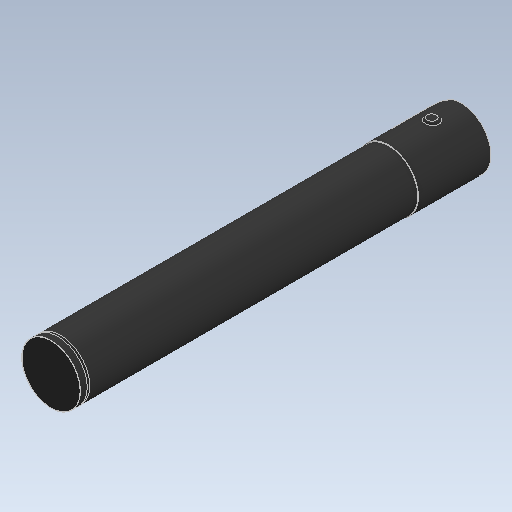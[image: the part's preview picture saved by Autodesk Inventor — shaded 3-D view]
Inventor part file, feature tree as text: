
AUTODESK INVENTOR PART (.ipt)
format: ipt  version: 2021 (Build 250183000, 183)  size: 203,264 bytes
history: native  units: mm
features: extrude x6, sketch x6, fillet x4, plane x1, projected_geometry x1
ambient origin geometry x8: Origin, YZ Plane, XZ Plane, XY Plane, X Axis, Y Axis, Z Axis, Center Point
bodies: Solid1 (feature_tree)
feature tree (18):
  extrude  "Extrusion1"  Depth=89.9mm TaperAngle=0.0deg
  plane  "Work Plane1"
  extrude  "Extrusion2"  Depth=0.5mm
  fillet  "Fillet1"  Radius=0.2mm
  fillet  "Fillet2"  Radius=1.0mm
  extrude  "Extrusion3"  Depth=12.0mm
  extrude  "Extrusion4"  Depth=2.0mm
  extrude  "Extrusion5"  TaperAngle=0.0deg  [1 undecoded]
  extrude  "Extrusion6"  Depth=3.0mm TaperAngle=0.0deg
  fillet  "Fillet3"  Radius=1.0mm
  fillet  "Fillet4"  Radius=74.0mm
  sketch  "Sketch1"  dims[d0=13.2mm d1=89.9mm d2=0.0mm]
  sketch  "Sketch2"  dims[d3=-1.5mm d4=0.5mm d5=0.2mm d6=0.0mm d7=1.0mm]
  sketch  "Sketch3"  dims[d8=0.2mm d9=12.0mm]
  projected_geometry  "Projected Loop1"
  sketch  "Sketch4"  dims[d10=45.0deg d11=2.0mm]
  sketch  "Sketch5"  dims[d12=3.490659mm d13=0.0mm d14=0.0mm]
  sketch  "Sketch6"  dims[d15=12.9mm d16=74.0mm d17=0.0mm d18=1.0mm d19=74.0mm d20=0.0mm d21=6.35mm d22=3.0mm d23=14.0mm d24=0.0mm d25=0.5mm d26=3.0mm]
note: 1 required parameter value undecoded (feature->parameter linkage not recoverable at this tier; creation-order binding heuristic only, values carry confidence <= 0.55)
